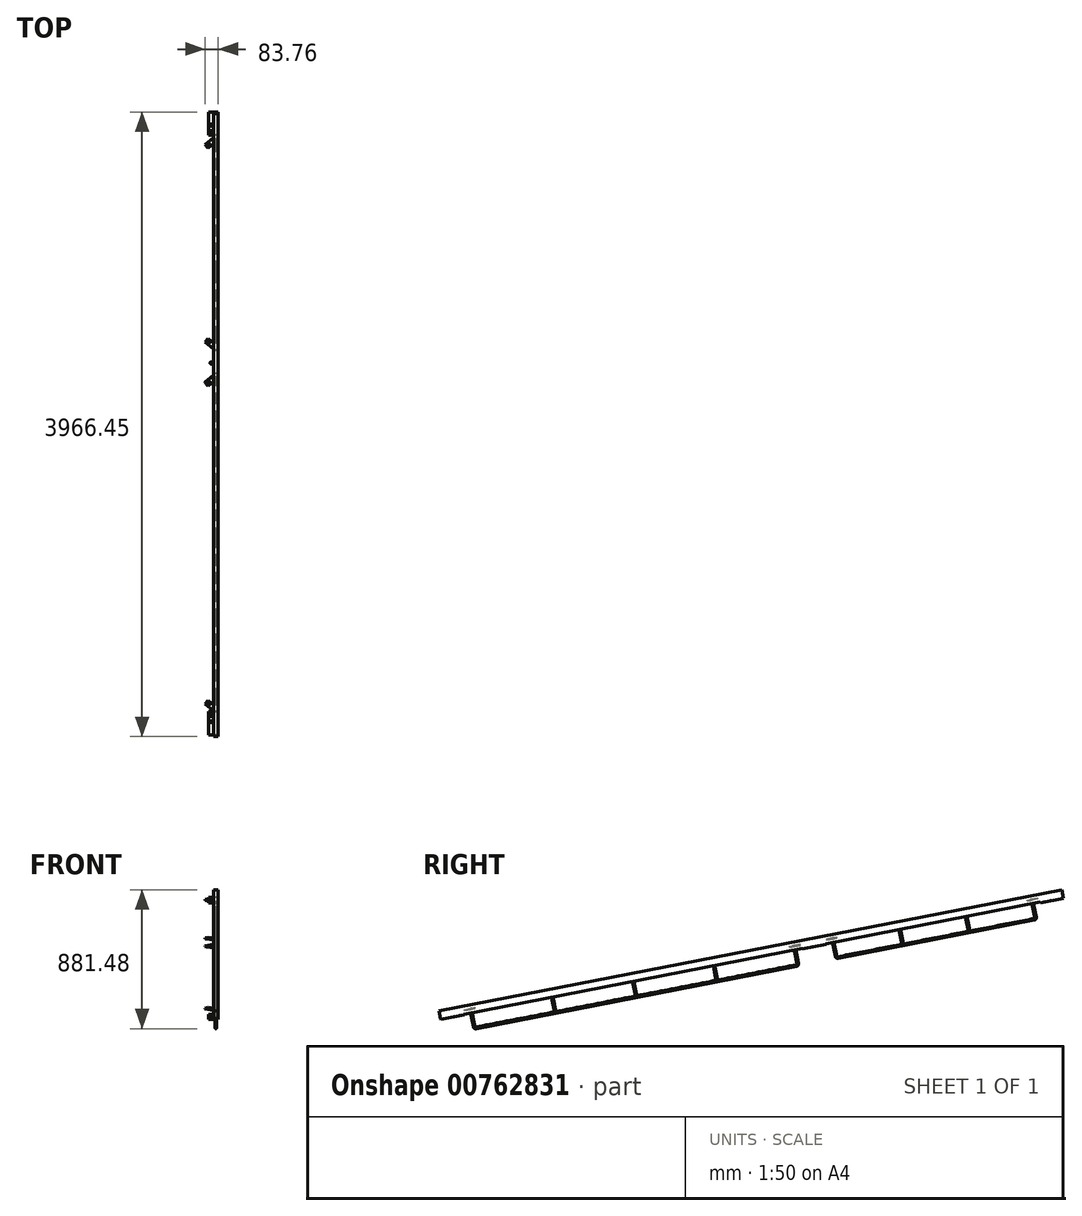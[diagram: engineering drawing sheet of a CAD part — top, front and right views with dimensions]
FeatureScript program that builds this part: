
annotation { "Feature Type Name" : "Feature", "Feature Type Description" : "" }
export const myFeature = defineFeature(function(context is Context, id is Id, definition is map)
    precondition{}
    {
        {
            var Q0;
            Q0=qCreatedBy(makeId("Top.planeOp"),FACE);
            var sketch = newSketch(context, id + "F0", { "sketchPlane" : qUnion([Q0])});
            skPoint(sketch, "E0", {"position": v(0, 0) * mm});
            skPoint(sketch, "E1", {"position": v(28.11, 0) * mm});
            skLineSegment(sketch, "E2", {"start": v(0, 0) * mm, "end": v(28.11, 0) * mm});
            skSolve(sketch);
        }
        {
            var Q0;
            Q0=qCreatedBy(makeId("Top.planeOp"),FACE);
            var Q1;
            Q1=sQuery(id+"F0.wireOp",EDGE,"E2");
            cPlane(context, id + "F1", {"entities" : qUnion([Q0, Q1]), "cplaneType" : CPlaneType.LINE_ANGLE, "offset" : 25 * mm, "angle" : 11 * degree, "width" : 150 * mm, "height" : 150 * mm});
        }
        {
            var Q0;
            Q0=qCreatedBy(id+"F1.planeOp",FACE);
            var Q1;
            Q1=sQuery(id+"F0.wireOp",EDGE,"E2");
            cPlane(context, id + "F2", {"entities" : qUnion([Q0, Q1]), "cplaneType" : CPlaneType.LINE_ANGLE, "offset" : 25 * mm, "angle" : 90 * degree, "width" : 150 * mm, "height" : 150 * mm});
        }
        {
            var Q0;
            Q0=qCreatedBy(id+"F2.planeOp",FACE);
            var sketch = newSketch(context, id + "F3", { "sketchPlane" : qUnion([Q0])});
            skLineSegment(sketch, "E3.bottom", {"start": v(15, -25) * mm, "end": v(-15, -25) * mm});
            skLineSegment(sketch, "E3.top", {"start": v(15, 25) * mm, "end": v(-15, 25) * mm});
            skLineSegment(sketch, "E3.left", {"start": v(15, -25) * mm, "end": v(15, 25) * mm});
            skLineSegment(sketch, "E3.right", {"start": v(-15, -25) * mm, "end": v(-15, 25) * mm});
            skPoint(sketch, "E3.middle", {"position": v(0, 0) * mm});
            skLineSegment(sketch, "E4.bottom", {"start": v(14, -24) * mm, "end": v(-14, -24) * mm});
            skLineSegment(sketch, "E4.top", {"start": v(14, 24) * mm, "end": v(-14, 24) * mm});
            skLineSegment(sketch, "E4.left", {"start": v(14, -24) * mm, "end": v(14, 24) * mm});
            skLineSegment(sketch, "E4.right", {"start": v(-14, -24) * mm, "end": v(-14, 24) * mm});
            skSolve(sketch);
        }
        {
            var Q0;
            Q0=qSketchRegion(id+"F3",true);
            extrude(context, id + "F4", {"entities" : qUnion([Q0]), "depth" : 30 * mm, "offsetDistance" : 25 * mm, "hasSecondDirection" : true, "secondDirectionOppositeDirection" : true, "secondDirectionDepth" : 4000 * mm});
        }
        {
            var Q0;
            Q0=makeQuery(id+"F4.opExtrude","SWEPT_FACE",FACE,{"disambiguationData":[OSD([sQuery(id+"F3.wireOp",EDGE,"E3.bottom")])]});
            var sketch = newSketch(context, id + "F5", { "sketchPlane" : qUnion([Q0])});
            skLineSegment(sketch, "E5.0", {"start": v(45, -4000) * mm, "end": v(135, -4000) * mm});
            skLineSegment(sketch, "E6.0", {"start": v(-15, -4000) * mm, "end": v(45, -4000) * mm});
            skLineSegment(sketch, "E7.0", {"start": v(-15, -4000) * mm, "end": v(-15, -3850) * mm});
            skLineSegment(sketch, "E8.0", {"start": v(-15, -3850) * mm, "end": v(45, -3850) * mm, "construction": true});
            skLineSegment(sketch, "E9.0", {"start": v(45, -3940) * mm, "end": v(45, -3850) * mm, "construction": true});
            skLineSegment(sketch, "E10.0", {"start": v(45, -3940) * mm, "end": v(135, -3940) * mm, "construction": true});
            skLineSegment(sketch, "E11.0", {"start": v(135, -4000) * mm, "end": v(135, -3940) * mm});
            skCircle(sketch, "E12.0", {"center": v(70, -3955) * mm, "radius": 6 * mm});
            skCircle(sketch, "E13.0", {"center": v(110, -3955) * mm, "radius": 6 * mm, "construction": true});
            skCircle(sketch, "E14.0", {"center": v(30, -3915) * mm, "radius": 6 * mm, "construction": true});
            skCircle(sketch, "E15.0", {"center": v(30, -3875) * mm, "radius": 6 * mm, "construction": true});
            skLineSegment(sketch, "E16", {"start": v(45, -3940) * mm, "end": v(45, -4000) * mm, "construction": true});
            skLineSegment(sketch, "E17", {"start": v(-15, -4000) * mm, "end": v(15, -4000) * mm, "construction": true});
            skLineSegment(sketch, "E18", {"start": v(15, -4000) * mm, "end": v(0, -4000) * mm, "construction": true});
            skLineSegment(sketch, "E19", {"start": v(0, -4000) * mm, "end": v(0, -3914.13) * mm, "construction": true});
            skLineSegment(sketch, "E20.MirrorCS", {"start": v(-45, -3940) * mm, "end": v(-45, -4000) * mm});
            skLineSegment(sketch, "E21.MirrorCS", {"start": v(-45, -3940) * mm, "end": v(-45, -3850) * mm});
            skCircle(sketch, "E22.MirrorC", {"center": v(-30, -3915) * mm, "radius": 6 * mm});
            skCircle(sketch, "E23.MirrorC", {"center": v(-30, -3875) * mm, "radius": 6 * mm});
            skLineSegment(sketch, "E24.MirrorCS", {"start": v(15, -3850) * mm, "end": v(-45, -3850) * mm});
            skLineSegment(sketch, "E25.MirrorCS", {"start": v(15, -4000) * mm, "end": v(-45, -4000) * mm});
            skSolve(sketch);
        }
        {
            var Q0;
            {var subQ0=sQuery(id+"F5.wireOp",EDGE,"E9.0");Q0=makeQuery(id+"F5.imprint","IMPRINT",FACE,{"disambiguationData":[TD([[makeQuery(id+"F5.imprint","IMPRINT",EDGE,{"derivedFrom":subQ0}),1.0]])]});}
            var Q1;
            {var subQ4=sQuery(id+"F5.wireOp",EDGE,"E7.0");Q1=makeQuery(id+"F5.imprint","IMPRINT",FACE,{"disambiguationData":[TD([[makeQuery(id+"F5.imprint","IMPRINT",EDGE,{"derivedFrom":subQ4}),1.0]])]});}
            var Q2;
            {var subQ2=sQuery(id+"F5.wireOp",EDGE,"E7.0");Q2=makeQuery(id+"F5.imprint","IMPRINT",FACE,{"disambiguationData":[TD([[makeQuery(id+"F5.imprint","IMPRINT",EDGE,{"derivedFrom":subQ2}),-1.0]])]});}
            extrude(context, id + "F6", {"entities" : qUnion([Q0, Q1, Q2]), "operationType" : NewBodyOperationType.ADD, "depth" : 5 * mm, "offsetDistance" : 25 * mm});
        }
        {
            var Q0;
            Q0=makeQuery(id+"F4.opExtrude","SWEPT_FACE",FACE,{"disambiguationData":[OSD([sQuery(id+"F3.wireOp",EDGE,"E3.bottom")])]});
            var sketch = newSketch(context, id + "F7", { "sketchPlane" : qUnion([Q0])});
            skLineSegment(sketch, "E26.0", {"start": v(45, -2401.65) * mm, "end": v(45, -2311.65) * mm});
            skLineSegment(sketch, "E27.0", {"start": v(-15, -2311.65) * mm, "end": v(45, -2311.65) * mm});
            skLineSegment(sketch, "E28.0", {"start": v(-15, -2461.65) * mm, "end": v(135, -2461.65) * mm});
            skLineSegment(sketch, "E29.0", {"start": v(135, -2461.65) * mm, "end": v(135, -2401.65) * mm});
            skLineSegment(sketch, "E30.0", {"start": v(45, -2401.65) * mm, "end": v(135, -2401.65) * mm});
            skLineSegment(sketch, "E31", {"start": v(-15, -2461.65) * mm, "end": v(-15, -2311.65) * mm});
            skLineSegment(sketch, "E32", {"start": v(45, -2401.65) * mm, "end": v(45, -2461.65) * mm});
            skCircle(sketch, "E33.0", {"center": v(30, -2376.65) * mm, "radius": 6 * mm});
            skCircle(sketch, "E34.0", {"center": v(30, -2336.65) * mm, "radius": 6 * mm});
            skLineSegment(sketch, "E35", {"start": v(-15, -2461.65) * mm, "end": v(15, -2461.65) * mm, "construction": true});
            skLineSegment(sketch, "E36", {"start": v(15, -2461.65) * mm, "end": v(0, -2461.65) * mm, "construction": true});
            skLineSegment(sketch, "E37", {"start": v(0, -2461.65) * mm, "end": v(0, -2311.65) * mm, "construction": true});
            skCircle(sketch, "E38.MirrorC", {"center": v(-30, -2376.65) * mm, "radius": 6 * mm});
            skCircle(sketch, "E39.MirrorC", {"center": v(-30, -2336.65) * mm, "radius": 6 * mm});
            skLineSegment(sketch, "E40.MirrorCS", {"start": v(-45, -2401.65) * mm, "end": v(-45, -2311.65) * mm});
            skLineSegment(sketch, "E41.MirrorCS", {"start": v(15, -2311.65) * mm, "end": v(-45, -2311.65) * mm});
            skLineSegment(sketch, "E42.MirrorCS", {"start": v(15, -2461.65) * mm, "end": v(-135, -2461.65) * mm});
            skLineSegment(sketch, "E43.MirrorCS", {"start": v(-45, -2401.65) * mm, "end": v(-45, -2461.65) * mm});
            skSolve(sketch);
        }
        {
            var Q0;
            {var subQ0=sQuery(id+"F7.wireOp",EDGE,"E31");Q0=makeQuery(id+"F7.imprint","IMPRINT",FACE,{"disambiguationData":[TD([[makeQuery(id+"F7.imprint","IMPRINT",EDGE,{"derivedFrom":subQ0}),1.0]])]});}
            var Q1;
            {var subQ7=sQuery(id+"F7.wireOp",EDGE,"E26.0");Q1=makeQuery(id+"F7.imprint","IMPRINT",FACE,{"disambiguationData":[TD([[makeQuery(id+"F7.imprint","IMPRINT",EDGE,{"derivedFrom":subQ7}),1.0]])]});}
            extrude(context, id + "F8", {"entities" : qUnion([Q0, Q1]), "operationType" : NewBodyOperationType.ADD, "depth" : 5 * mm, "offsetDistance" : 25 * mm});
        }
        {
            var Q0;
            {var subQ3=sQuery(id+"F3.wireOp",EDGE,"E3.bottom");var subQ4=sQuery(id+"F7.wireOp",EDGE,"E27.0");Q0=makeQuery(id+"F8.boolean.opBoolean","SPLIT",FACE,{"disambiguationData":[TD([makeQuery(id+"F8.opExtrude","SWEPT_FACE",FACE,{"disambiguationData":[OSD([subQ4])]})])],"derivedFrom":makeQuery(id+"F4.opExtrude","SWEPT_FACE",FACE,{"disambiguationData":[OSD([subQ3])]})});}
            var sketch = newSketch(context, id + "F9", { "sketchPlane" : qUnion([Q0])});
            skLineSegment(sketch, "E44", {"start": v(-15, -120.03) * mm, "end": v(-15, 29) * mm});
            skLineSegment(sketch, "E45", {"start": v(45, 29.97) * mm, "end": v(45, 30) * mm});
            skLineSegment(sketch, "E46", {"start": v(0, -120.03) * mm, "end": v(0, 30) * mm, "construction": true});
            skCircle(sketch, "E47.MirrorC", {"center": v(-30, -95.03) * mm, "radius": 6 * mm});
            skCircle(sketch, "E48.MirrorC", {"center": v(-30, -55.03) * mm, "radius": 6 * mm});
            skLineSegment(sketch, "E49.MirrorCS", {"start": v(-45, 29.97) * mm, "end": v(-45, -120.03) * mm});
            skLineSegment(sketch, "E50", {"start": v(15, 30) * mm, "end": v(15, -120.03) * mm});
            skLineSegment(sketch, "E51", {"start": v(-15, -120.03) * mm, "end": v(-45, -120.03) * mm});
            skLineSegment(sketch, "E52", {"start": v(-45, 29.97) * mm, "end": v(15, 30) * mm});
            skLineSegment(sketch, "E53", {"start": v(15, -120.03) * mm, "end": v(-15, -120.03) * mm});
            skSolve(sketch);
        }
        {
            var Q0;
            Q0=qSketchRegion(id+"F9",true);
            extrude(context, id + "F10", {"entities" : qUnion([Q0]), "operationType" : NewBodyOperationType.ADD, "depth" : 4.8 * mm, "offsetDistance" : 25 * mm});
        }
        {
            var Q0;
            Q0=qCreatedBy(id+"F1.planeOp",FACE);
            var sketch = newSketch(context, id + "F11", { "sketchPlane" : qUnion([Q0])});
            skLineSegment(sketch, "E54", {"start": v(41, -1985.01) * mm, "end": v(15.07, -1985.01) * mm});
            skLineSegment(sketch, "E55", {"start": v(15, -2301.65) * mm, "end": v(15, -130.03) * mm});
            skLineSegment(sketch, "E56", {"start": v(45.74, -1215.84) * mm, "end": v(15, -1215.84) * mm});
            skLineSegment(sketch, "E57", {"start": v(15, -2471.65) * mm, "end": v(15, -3840) * mm});
            skLineSegment(sketch, "E58", {"start": v(29.54, -3155.82) * mm, "end": v(15, -3155.82) * mm});
            skLineSegment(sketch, "E59.MirrorCS", {"start": v(-68.76, -175.02) * mm, "end": v(-49.47, -198) * mm});
            skLineSegment(sketch, "E60.MirrorCS", {"start": v(-43.4, -173.32) * mm, "end": v(-59.12, -186.5) * mm, "construction": true});
            skCircle(sketch, "E61.MirrorC", {"center": v(-43.4, -173.32) * mm, "radius": 6 * mm});
            skLineSegment(sketch, "E62.MirrorCS", {"start": v(-15, -129.92) * mm, "end": v(-68.76, -175.02) * mm});
            skLineSegment(sketch, "E63.MirrorCS", {"start": v(-49.47, -2233.67) * mm, "end": v(-15, -2262.6) * mm});
            skLineSegment(sketch, "E64.MirrorCS", {"start": v(-15, -2301.65) * mm, "end": v(-68.63, -2256.65) * mm});
            skCircle(sketch, "E65.MirrorC", {"center": v(-43.4, -2258.35) * mm, "radius": 6 * mm});
            skLineSegment(sketch, "E66.MirrorCS", {"start": v(-14.97, -2471.64) * mm, "end": v(-68.6, -2516.64) * mm});
            skLineSegment(sketch, "E67.MirrorCS", {"start": v(-49.31, -2539.62) * mm, "end": v(-14.84, -2510.7) * mm});
            skCircle(sketch, "E68.MirrorC", {"center": v(-43.4, -2514.94) * mm, "radius": 6 * mm});
            skLineSegment(sketch, "E69.MirrorCS", {"start": v(-49.47, -3772.03) * mm, "end": v(-15, -3800.95) * mm});
            skCircle(sketch, "E70.MirrorC", {"center": v(-43.4, -3796.7) * mm, "radius": 6 * mm});
            skLineSegment(sketch, "E71", {"start": v(-15, -3840) * mm, "end": v(-15, -3800.95) * mm});
            skLineSegment(sketch, "E72", {"start": v(-14.84, -2510.7) * mm, "end": v(-14.97, -2471.64) * mm});
            skLineSegment(sketch, "E73", {"start": v(-15, -129.92) * mm, "end": v(-15, -168.98) * mm});
            skLineSegment(sketch, "E74", {"start": v(-15, -168.98) * mm, "end": v(-49.47, -198) * mm});
            skLineSegment(sketch, "E75", {"start": v(-15, -2262.6) * mm, "end": v(-15, -2301.65) * mm});
            skLineSegment(sketch, "E76", {"start": v(-49.47, -2233.67) * mm, "end": v(-68.63, -2256.65) * mm});
            skLineSegment(sketch, "E77", {"start": v(-68.6, -2516.64) * mm, "end": v(-49.31, -2539.62) * mm});
            skLineSegment(sketch, "E78", {"start": v(-49.47, -3772.03) * mm, "end": v(-68.76, -3795) * mm});
            skLineSegment(sketch, "E79", {"start": v(-15, -3840) * mm, "end": v(-68.76, -3795) * mm});
            skSolve(sketch);
        }
        {
            var Q0;
            Q0=makeQuery(id+"F11.imprint","IMPRINT",FACE,{"disambiguationData":[TD([[makeQuery(id+"F11.imprint","IMPRINT",EDGE,{"derivedFrom":sQuery(id+"F11.wireOp",EDGE,"E59.MirrorCS")}),1.0]])]});
            var Q1;
            Q1=makeQuery(id+"F11.imprint","IMPRINT",FACE,{"disambiguationData":[TD([[makeQuery(id+"F11.imprint","IMPRINT",EDGE,{"derivedFrom":sQuery(id+"F11.wireOp",EDGE,"E63.MirrorCS")}),-1.0]])]});
            var Q2;
            Q2=makeQuery(id+"F11.imprint","IMPRINT",FACE,{"disambiguationData":[TD([[makeQuery(id+"F11.imprint","IMPRINT",EDGE,{"derivedFrom":sQuery(id+"F11.wireOp",EDGE,"E66.MirrorCS")}),1.0]])]});
            var Q3;
            Q3=makeQuery(id+"F11.imprint","IMPRINT",FACE,{"disambiguationData":[TD([[makeQuery(id+"F11.imprint","IMPRINT",EDGE,{"derivedFrom":sQuery(id+"F11.wireOp",EDGE,"E69.MirrorCS")}),-1.0]])]});
            extrude(context, id + "F12", {"entities" : qUnion([Q0, Q1, Q2, Q3]), "operationType" : NewBodyOperationType.ADD, "depth" : 2.5 * mm, "offsetDistance" : 25 * mm, "hasSecondDirection" : true, "secondDirectionOppositeDirection" : true, "secondDirectionDepth" : 2.5 * mm});
        }
        {
            var Q0;
            Q0=qCreatedBy(makeId("Right.planeOp"),FACE);
            var sketch = newSketch(context, id + "F13", { "sketchPlane" : qUnion([Q0])});
            skLineSegment(sketch, "E80", {"start": v(166.55, 29.83) * mm, "end": v(170.85, 7.74) * mm});
            skLineSegment(sketch, "E81", {"start": v(170.85, 7.74) * mm, "end": v(188.02, -80.6) * mm});
            skLineSegment(sketch, "E82", {"start": v(188.02, -80.6) * mm, "end": v(197.84, -78.7) * mm});
            skArc(sketch, "E83", {"start": v(188.02, -80.6) * mm, "mid": v(192.24, -86.99) * mm, "end": v(199.74, -88.51) * mm});
            skLineSegment(sketch, "E84", {"start": v(197.84, -78.7) * mm, "end": v(199.74, -88.51) * mm, "construction": true});
            skPoint(sketch, "E85.0", {"position": v(166.55, 29.83) * mm});
            skPoint(sketch, "E86.0", {"position": v(165.6, 34.74) * mm});
            skLineSegment(sketch, "E87", {"start": v(165.6, 34.74) * mm, "end": v(166.55, 29.83) * mm});
            skPoint(sketch, "E88.0", {"position": v(2221.4, 429.25) * mm});
            skPoint(sketch, "E89.0", {"position": v(2220.44, 434.16) * mm});
            skLineSegment(sketch, "E90", {"start": v(2220.44, 434.16) * mm, "end": v(2221.4, 429.25) * mm});
            skLineSegment(sketch, "E91", {"start": v(2221.4, 429.25) * mm, "end": v(2225.69, 407.16) * mm});
            skLineSegment(sketch, "E92", {"start": v(2225.69, 407.16) * mm, "end": v(2242.86, 318.82) * mm});
            skLineSegment(sketch, "E93", {"start": v(2242.86, 318.82) * mm, "end": v(2233.04, 316.9) * mm, "construction": true});
            skArc(sketch, "E94", {"start": v(2234.95, 307.1) * mm, "mid": v(2241.33, 311.32) * mm, "end": v(2242.86, 318.82) * mm});
            skLineSegment(sketch, "E95", {"start": v(2233.04, 316.9) * mm, "end": v(2234.95, 307.1) * mm});
            skLineSegment(sketch, "E96", {"start": v(1217.35, 109.29) * mm, "end": v(1198.27, 207.45) * mm});
            skLineSegment(sketch, "E97", {"start": v(1731.06, 209.14) * mm, "end": v(1711.98, 307.3) * mm});
            skLineSegment(sketch, "E98", {"start": v(703.64, 9.43) * mm, "end": v(684.56, 107.6) * mm});
            skLineSegment(sketch, "E99", {"start": v(199.74, -88.51) * mm, "end": v(2234.95, 307.1) * mm});
            skPoint(sketch, "E100.0", {"position": v(2465.15, 476.63) * mm});
            skPoint(sketch, "E101.0", {"position": v(2464.2, 481.54) * mm});
            skPoint(sketch, "E102.0", {"position": v(3730.53, 727.69) * mm});
            skPoint(sketch, "E103.0", {"position": v(3731.49, 722.78) * mm});
            skLineSegment(sketch, "E104", {"start": v(3730.53, 727.69) * mm, "end": v(3731.49, 722.78) * mm});
            skLineSegment(sketch, "E105", {"start": v(2465.15, 476.63) * mm, "end": v(2464.2, 481.54) * mm});
            skLineSegment(sketch, "E106", {"start": v(2465.15, 476.63) * mm, "end": v(2469.44, 454.54) * mm});
            skLineSegment(sketch, "E107", {"start": v(3731.49, 722.78) * mm, "end": v(3735.78, 700.7) * mm});
            skLineSegment(sketch, "E108", {"start": v(3735.78, 700.7) * mm, "end": v(3752.95, 612.35) * mm});
            skLineSegment(sketch, "E109", {"start": v(3752.95, 612.35) * mm, "end": v(3743.13, 610.44) * mm});
            skArc(sketch, "E110", {"start": v(3745.04, 600.62) * mm, "mid": v(3751.43, 604.85) * mm, "end": v(3752.95, 612.35) * mm});
            skLineSegment(sketch, "E111", {"start": v(3743.13, 610.44) * mm, "end": v(3745.04, 600.62) * mm, "construction": true});
            skLineSegment(sketch, "E112", {"start": v(2469.44, 454.54) * mm, "end": v(2486.62, 366.2) * mm});
            skLineSegment(sketch, "E113", {"start": v(2486.62, 366.2) * mm, "end": v(2496.43, 368.1) * mm});
            skArc(sketch, "E114", {"start": v(2486.62, 366.2) * mm, "mid": v(2490.9, 359.77) * mm, "end": v(2498.5, 358.32) * mm});
            skLineSegment(sketch, "E115", {"start": v(2496.43, 368.1) * mm, "end": v(2498.34, 358.29) * mm, "construction": true});
            skLineSegment(sketch, "E116", {"start": v(2469.44, 454.54) * mm, "end": v(2891.56, 536.6) * mm, "construction": true});
            skLineSegment(sketch, "E117", {"start": v(2891.56, 536.6) * mm, "end": v(3313.67, 618.64) * mm, "construction": true});
            skLineSegment(sketch, "E118", {"start": v(3313.67, 618.64) * mm, "end": v(3333.52, 520.63) * mm});
            skLineSegment(sketch, "E119", {"start": v(2891.56, 536.6) * mm, "end": v(2911.46, 438.6) * mm});
            skLineSegment(sketch, "E120", {"start": v(3313.67, 618.64) * mm, "end": v(3735.78, 700.7) * mm, "construction": true});
            skLineSegment(sketch, "E121", {"start": v(170.85, 7.74) * mm, "end": v(684.56, 107.6) * mm, "construction": true});
            skLineSegment(sketch, "E122", {"start": v(1198.27, 207.45) * mm, "end": v(684.56, 107.6) * mm, "construction": true});
            skLineSegment(sketch, "E123", {"start": v(1198.27, 207.45) * mm, "end": v(1711.98, 307.3) * mm, "construction": true});
            skLineSegment(sketch, "E124", {"start": v(1711.98, 307.3) * mm, "end": v(2225.69, 407.16) * mm, "construction": true});
            skLineSegment(sketch, "E125", {"start": v(2498.5, 358.32) * mm, "end": v(3745.04, 600.62) * mm});
            skSolve(sketch);
        }
        {
            var Q0;
            {var subQ7=sQuery(id+"F7.wireOp",EDGE,"E27.0");var subQ9=makeQuery(id+"F8.opExtrude","SWEPT_FACE",FACE,{"disambiguationData":[OSD([subQ7])]});var subQ12=sQuery(id+"F3.wireOp",EDGE,"E3.bottom");Q0=makeQuery(id+"F10.boolean.opBoolean","SPLIT",FACE,{"disambiguationData":[TD([subQ9])],"derivedFrom":makeQuery(id+"F8.boolean.opBoolean","SPLIT",FACE,{"disambiguationData":[TD([subQ9])],"derivedFrom":makeQuery(id+"F4.opExtrude","SWEPT_FACE",FACE,{"disambiguationData":[OSD([subQ12])]})})});}
            var sketch = newSketch(context, id + "F14", { "sketchPlane" : qUnion([Q0])});
            skCircle(sketch, "E126", {"center": v(0, -169.19) * mm, "radius": 5 * mm});
            skCircle(sketch, "E127", {"center": v(0, -692.51) * mm, "radius": 5 * mm});
            skCircle(sketch, "E128", {"center": v(0, -1215.84) * mm, "radius": 5 * mm});
            skCircle(sketch, "E129", {"center": v(0, -1739.16) * mm, "radius": 5 * mm});
            skCircle(sketch, "E130", {"center": v(0, -2262.49) * mm, "radius": 5 * mm});
            skCircle(sketch, "E131", {"center": v(0, -2510.8) * mm, "radius": 5 * mm});
            skCircle(sketch, "E132", {"center": v(0, -2940.82) * mm, "radius": 5 * mm});
            skCircle(sketch, "E133", {"center": v(0, -3370.83) * mm, "radius": 5 * mm});
            skCircle(sketch, "E134", {"center": v(0, -3800.84) * mm, "radius": 5 * mm});
            skSolve(sketch);
        }
        {
            var Q0;
            Q0=makeQuery(id+"F14.imprint","IMPRINT",FACE,{"disambiguationData":[TD([[makeQuery(id+"F14.imprint","IMPRINT",EDGE,{"derivedFrom":sQuery(id+"F14.wireOp",EDGE,"E126")}),1.0]])]});
            var Q1;
            Q1=sQuery(id+"F13.wireOp",EDGE,"E81");
            var Q2;
            Q2=sQuery(id+"F13.wireOp",EDGE,"E83");
            var Q3;
            Q3=sQuery(id+"F13.wireOp",EDGE,"E99");
            var Q4;
            Q4=sQuery(id+"F13.wireOp",EDGE,"E94");
            var Q5;
            Q5=sQuery(id+"F13.wireOp",EDGE,"E92");
            sweep(context, id + "F15", {"operationType" : NewBodyOperationType.ADD, "profiles" : qUnion([Q0]), "path" : qUnion([Q1, Q2, Q3, Q4, Q5])});
        }
        {
            var Q0;
            Q0=makeQuery(id+"F14.imprint","IMPRINT",FACE,{"disambiguationData":[TD([[makeQuery(id+"F14.imprint","IMPRINT",EDGE,{"derivedFrom":sQuery(id+"F14.wireOp",EDGE,"E127")}),1.0]])]});
            var Q1;
            Q1=sQuery(id+"F13.wireOp",EDGE,"E98");
            sweep(context, id + "F16", {"operationType" : NewBodyOperationType.ADD, "profiles" : qUnion([Q0]), "path" : qUnion([Q1])});
        }
        {
            var Q0;
            Q0=makeQuery(id+"F14.imprint","IMPRINT",FACE,{"disambiguationData":[TD([[makeQuery(id+"F14.imprint","IMPRINT",EDGE,{"derivedFrom":sQuery(id+"F14.wireOp",EDGE,"E128")}),1.0]])]});
            var Q1;
            Q1=sQuery(id+"F13.wireOp",EDGE,"E96");
            sweep(context, id + "F17", {"operationType" : NewBodyOperationType.ADD, "profiles" : qUnion([Q0]), "path" : qUnion([Q1])});
        }
        {
            var Q0;
            Q0=makeQuery(id+"F14.imprint","IMPRINT",FACE,{"disambiguationData":[TD([[makeQuery(id+"F14.imprint","IMPRINT",EDGE,{"derivedFrom":sQuery(id+"F14.wireOp",EDGE,"E129")}),1.0]])]});
            var Q1;
            Q1=sQuery(id+"F13.wireOp",EDGE,"E97");
            sweep(context, id + "F18", {"operationType" : NewBodyOperationType.ADD, "profiles" : qUnion([Q0]), "path" : qUnion([Q1])});
        }
        {
            var Q0;
            Q0=makeQuery(id+"F14.imprint","IMPRINT",FACE,{"disambiguationData":[TD([[makeQuery(id+"F14.imprint","IMPRINT",EDGE,{"derivedFrom":sQuery(id+"F14.wireOp",EDGE,"E131")}),1.0]])]});
            var Q1;
            Q1=sQuery(id+"F13.wireOp",EDGE,"E112");
            var Q2;
            Q2=sQuery(id+"F13.wireOp",EDGE,"E114");
            var Q3;
            Q3=sQuery(id+"F13.wireOp",EDGE,"E125");
            var Q4;
            Q4=sQuery(id+"F13.wireOp",EDGE,"E110");
            var Q5;
            Q5=sQuery(id+"F13.wireOp",EDGE,"E108");
            sweep(context, id + "F19", {"operationType" : NewBodyOperationType.ADD, "profiles" : qUnion([Q0]), "path" : qUnion([Q1, Q2, Q3, Q4, Q5])});
        }
        {
            var Q0;
            Q0=makeQuery(id+"F14.imprint","IMPRINT",FACE,{"disambiguationData":[TD([[makeQuery(id+"F14.imprint","IMPRINT",EDGE,{"derivedFrom":sQuery(id+"F14.wireOp",EDGE,"E132")}),1.0]])]});
            var Q1;
            Q1=sQuery(id+"F13.wireOp",EDGE,"E119");
            sweep(context, id + "F20", {"operationType" : NewBodyOperationType.ADD, "profiles" : qUnion([Q0]), "path" : qUnion([Q1])});
        }
        {
            var Q0;
            Q0=makeQuery(id+"F14.imprint","IMPRINT",FACE,{"disambiguationData":[TD([[makeQuery(id+"F14.imprint","IMPRINT",EDGE,{"derivedFrom":sQuery(id+"F14.wireOp",EDGE,"E133")}),1.0]])]});
            var Q1;
            Q1=sQuery(id+"F13.wireOp",EDGE,"E118");
            sweep(context, id + "F21", {"operationType" : NewBodyOperationType.ADD, "profiles" : qUnion([Q0]), "path" : qUnion([Q1])});
        }
        {
            var Q0;
            Q0=makeQuery(id+"F8.opExtrude","CAP_FACE",FACE,{"disambiguationData":[OSD([sQuery(id+"F7.wireOp",EDGE,"E26.0"),sQuery(id+"F7.wireOp",EDGE,"E27.0"),sQuery(id+"F7.wireOp",EDGE,"E28.0"),sQuery(id+"F7.wireOp",EDGE,"E31"),sQuery(id+"F7.wireOp",EDGE,"E32"),sQuery(id+"F7.wireOp",EDGE,"E33.0"),sQuery(id+"F7.wireOp",EDGE,"E34.0"),sQuery(id+"F7.wireOp",EDGE,"E41.MirrorCS"),sQuery(id+"F7.wireOp",EDGE,"E42.MirrorCS")])],"isStart":false});
            var sketch = newSketch(context, id + "F22", { "sketchPlane" : qUnion([Q0])});
            skLineSegment(sketch, "E135", {"start": v(-15, -2461.65) * mm, "end": v(15, -2461.65) * mm});
            skLineSegment(sketch, "E136", {"start": v(0, -2461.65) * mm, "end": v(0, -2410.46) * mm, "construction": true});
            skPoint(sketch, "E137.0", {"position": v(15, -2311.65) * mm});
            skCircle(sketch, "E138.MirrorC", {"center": v(-30, -2376.65) * mm, "radius": 6 * mm});
            skLineSegment(sketch, "E139.MirrorCS", {"start": v(-45, -2311.65) * mm, "end": v(-45, -2461.65) * mm});
            skCircle(sketch, "E140.MirrorC", {"center": v(-30, -2336.65) * mm, "radius": 6 * mm});
            skLineSegment(sketch, "E141", {"start": v(-15, -2461.65) * mm, "end": v(-45, -2461.65) * mm});
            skLineSegment(sketch, "E142", {"start": v(-45, -2311.65) * mm, "end": v(-15, -2311.65) * mm});
            skLineSegment(sketch, "E143", {"start": v(15, -2461.65) * mm, "end": v(15, -2311.65) * mm});
            skSolve(sketch);
        }
        {
            var Q0;
            Q0=makeQuery(id+"F22.imprint","IMPRINT",FACE,{"disambiguationData":[TD([[makeQuery(id+"F22.imprint","IMPRINT",EDGE,{"derivedFrom":sQuery(id+"F22.wireOp",EDGE,"E138.MirrorC")}),1.0]])]});
            extrude(context, id + "F23", {"entities" : qUnion([Q0]), "operationType" : NewBodyOperationType.ADD, "oppositeDirection" : true, "depth" : 5 * mm, "offsetDistance" : 25 * mm});
        }
        {
            var Q0;
            {var subQ0=sQuery(id+"F7.wireOp",EDGE,"E31");Q0=makeQuery(id+"F23.boolean.opBoolean","MERGE",FACE,{"derivedFrom":[makeQuery(id+"F8.opExtrude","CAP_FACE",FACE,{"disambiguationData":[OSD([sQuery(id+"F7.wireOp",EDGE,"E26.0"),sQuery(id+"F7.wireOp",EDGE,"E27.0"),sQuery(id+"F7.wireOp",EDGE,"E28.0"),subQ0,sQuery(id+"F7.wireOp",EDGE,"E32"),sQuery(id+"F7.wireOp",EDGE,"E33.0"),sQuery(id+"F7.wireOp",EDGE,"E34.0"),sQuery(id+"F7.wireOp",EDGE,"E41.MirrorCS"),sQuery(id+"F7.wireOp",EDGE,"E42.MirrorCS")])],"isStart":false}),makeQuery(id+"F23.opExtrude","CAP_FACE",FACE,{"disambiguationData":[OSD([subQ0,sQuery(id+"F22.wireOp",EDGE,"E138.MirrorC"),sQuery(id+"F22.wireOp",EDGE,"E139.MirrorCS"),sQuery(id+"F22.wireOp",EDGE,"E140.MirrorC"),sQuery(id+"F22.wireOp",EDGE,"E141"),sQuery(id+"F22.wireOp",EDGE,"E142")])],"isStart":true})]});}
            var sketch = newSketch(context, id + "F24", { "sketchPlane" : qUnion([Q0])});
            skLineSegment(sketch, "E144", {"start": v(45, -2461.65) * mm, "end": v(15, -2461.65) * mm});
            skLineSegment(sketch, "E145", {"start": v(15, -2461.65) * mm, "end": v(15, -2311.65) * mm});
            skLineSegment(sketch, "E146", {"start": v(15, -2311.65) * mm, "end": v(45, -2311.65) * mm});
            skLineSegment(sketch, "E147", {"start": v(45, -2311.65) * mm, "end": v(45, -2461.65) * mm});
            skSolve(sketch);
        }
        {
            var Q0;
            Q0 = qSketchRegion(id + "F24", true);
            extrude(context, id + "F25", {"entities" : qUnion([Q0]), "operationType" : NewBodyOperationType.REMOVE, "oppositeDirection" : true, "depth" : 25 * mm, "offsetDistance" : 25 * mm});
        }
    });
